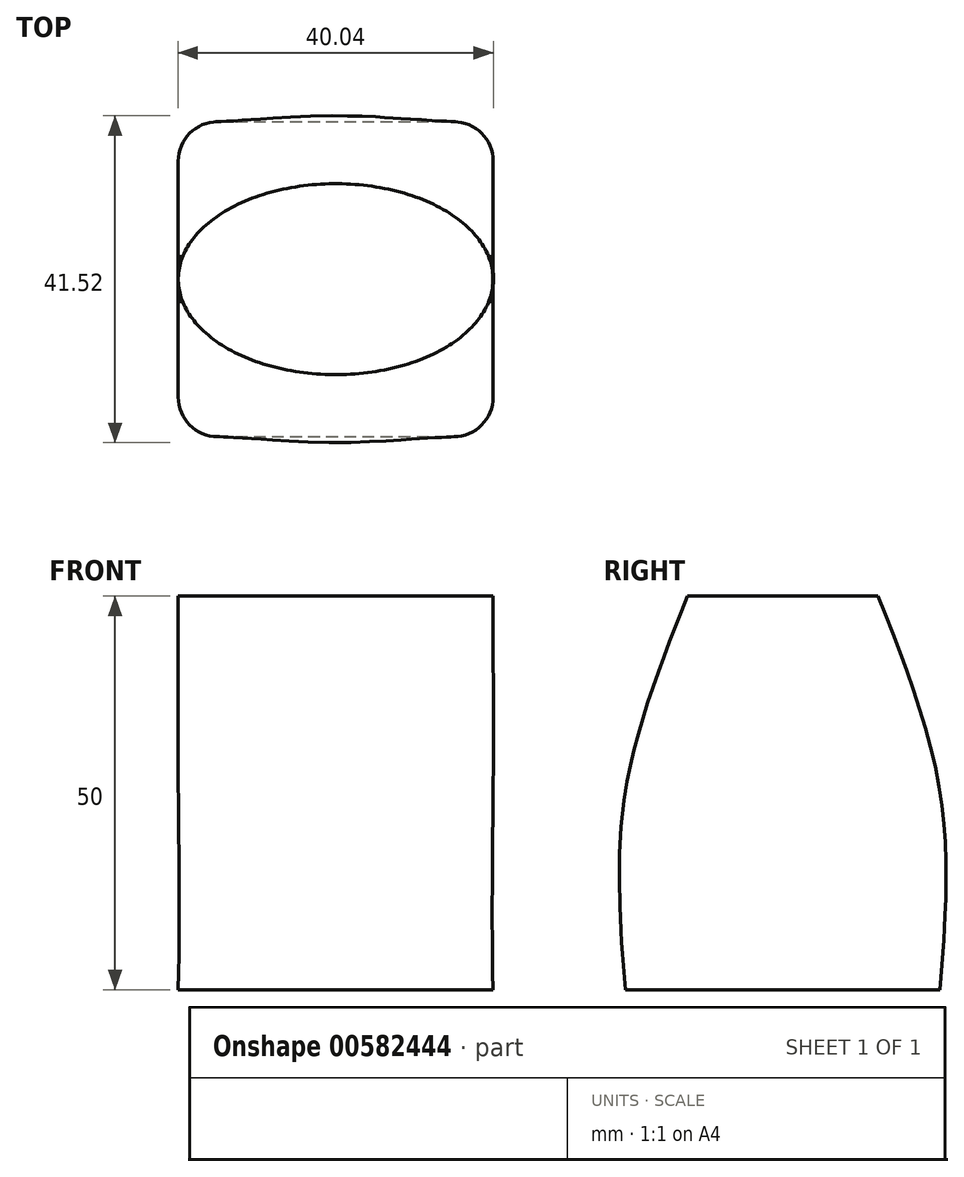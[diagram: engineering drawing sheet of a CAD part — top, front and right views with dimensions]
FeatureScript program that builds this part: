
annotation { "Feature Type Name" : "Feature", "Feature Type Description" : "" }
export const myFeature = defineFeature(function(context is Context, id is Id, definition is map)
    precondition{}
    {
        {
            var Q0;
            Q0=qCreatedBy(makeId("Top.planeOp"),FACE);
            var sketch = newSketch(context, id + "F0", { "sketchPlane" : qUnion([Q0])});
            skLineSegment(sketch, "E0.bottom", {"start": v(-15, 20) * mm, "end": v(15, 20) * mm});
            skLineSegment(sketch, "E0.top", {"start": v(-15, -20) * mm, "end": v(15, -20) * mm});
            skLineSegment(sketch, "E0.left", {"start": v(-20, 15) * mm, "end": v(-20, -15) * mm});
            skLineSegment(sketch, "E0.right", {"start": v(20, 15) * mm, "end": v(20, -15) * mm});
            skPoint(sketch, "E0.middle", {"position": v(0, 0) * mm});
            skPoint(sketch, "E1.visualSharp", {"position": v(-20, 20) * mm});
            skArc(sketch, "E1.filletArc", {"start": v(-15, 20) * mm, "mid": v(-18.54, 18.54) * mm, "end": v(-20, 15) * mm});
            skPoint(sketch, "E2.visualSharp", {"position": v(20, 20) * mm});
            skArc(sketch, "E2.filletArc", {"start": v(20, 15) * mm, "mid": v(18.54, 18.54) * mm, "end": v(15, 20) * mm});
            skPoint(sketch, "E3.visualSharp", {"position": v(20, -20) * mm});
            skArc(sketch, "E3.filletArc", {"start": v(15, -20) * mm, "mid": v(18.54, -18.54) * mm, "end": v(20, -15) * mm});
            skPoint(sketch, "E4.visualSharp", {"position": v(-20, -20) * mm});
            skArc(sketch, "E4.filletArc", {"start": v(-20, -15) * mm, "mid": v(-18.54, -18.54) * mm, "end": v(-15, -20) * mm});
            skSolve(sketch);
        }
        {
            var Q0;
            Q0=qCreatedBy(makeId("Top.planeOp"),FACE);
            cPlane(context, id + "F1", {"entities" : qUnion([Q0]), "cplaneType" : CPlaneType.OFFSET, "offset" : 25 * mm, "width" : 150 * mm, "height" : 150 * mm});
        }
        {
            var Q0;
            Q0=qCreatedBy(id+"F1.planeOp",FACE);
            cPlane(context, id + "F2", {"entities" : qUnion([Q0]), "cplaneType" : CPlaneType.OFFSET, "offset" : 25 * mm, "width" : 150 * mm, "height" : 150 * mm});
        }
        {
            var Q0;
            Q0=qCreatedBy(id+"F1.planeOp",FACE);
            var sketch = newSketch(context, id + "F3", { "sketchPlane" : qUnion([Q0])});
            skCircle(sketch, "E5", {"center": v(0, 0) * mm, "radius": 20 * mm});
            skSolve(sketch);
        }
        {
            var Q0;
            Q0=qCreatedBy(id+"F2.planeOp",FACE);
            var sketch = newSketch(context, id + "F4", { "sketchPlane" : qUnion([Q0])});
            skEllipse(sketch, "E6", {"center": v(0, 0) * mm, "majorRadius": 20 * mm, "minorRadius": 12.12 * mm, "majorAxis": v(-1, 0)});
            skSolve(sketch);
        }
        {
            var Q0;
            Q0=qCreatedBy(makeId("Front.planeOp"),FACE);
            var sketch = newSketch(context, id + "F5", { "sketchPlane" : qUnion([Q0])});
            skFitSpline(sketch, "E7", {"points": [v(-20, 50) * mm, v(-20, 25) * mm, v(-20, 0) * mm], "startDerivative": vector(0.05, -50.06) * mm, "endDerivative": vector(-1.44, -49.85) * mm});
            skLineSegment(sketch, "E8", {"start": v(0, 50) * mm, "end": v(0, 0) * mm, "construction": true});
            skFitSpline(sketch, "E9.MirrorCS", {"points": [v(20, 50) * mm, v(20, 25) * mm, v(20, 0) * mm], "startDerivative": vector(-0.05, -50.06) * mm, "endDerivative": vector(1.44, -49.85) * mm});
            skSolve(sketch);
        }
        {
            var Q0;
            Q0=makeQuery(id+"F0.imprint","IMPRINT",FACE,{"disambiguationData":[TD([[makeQuery(id+"F0.imprint","IMPRINT",EDGE,{"derivedFrom":sQuery(id+"F0.wireOp",EDGE,"E0.bottom")}),-1.0]])]});
            var Q1;
            Q1=makeQuery(id+"F3.imprint","IMPRINT",FACE,{"disambiguationData":[TD([[makeQuery(id+"F3.imprint","IMPRINT",EDGE,{"derivedFrom":sQuery(id+"F3.wireOp",EDGE,"E5")}),1.0]])]});
            var Q2;
            Q2=makeQuery(id+"F4.imprint","IMPRINT",FACE,{"disambiguationData":[TD([[makeQuery(id+"F4.imprint","IMPRINT",EDGE,{"derivedFrom":sQuery(id+"F4.wireOp",EDGE,"E6")}),1.0]])]});
            var Q3;
            Q3=sQuery(id+"F5.wireOp",EDGE,"E7");
            var Q4;
            Q4=sQuery(id+"F5.wireOp",EDGE,"E9.MirrorCS");
            loft(context, id + "F6", {"addGuides" : true, "sheetProfilesArray" : [{ "sheetProfileEntities" : qUnion([Q0]) }, { "sheetProfileEntities" : qUnion([Q1]) }, { "sheetProfileEntities" : qUnion([Q2]) }], "guidesArray" : [{ "guideEntities" : qUnion([Q3]), "guideDerivativeType" : LoftGuideDerivativeType.DEFAULT, "guideDerivativeMagnitude" : 1 }, { "guideEntities" : qUnion([Q4]), "guideDerivativeType" : LoftGuideDerivativeType.DEFAULT, "guideDerivativeMagnitude" : 1 }]});
        }
    });
